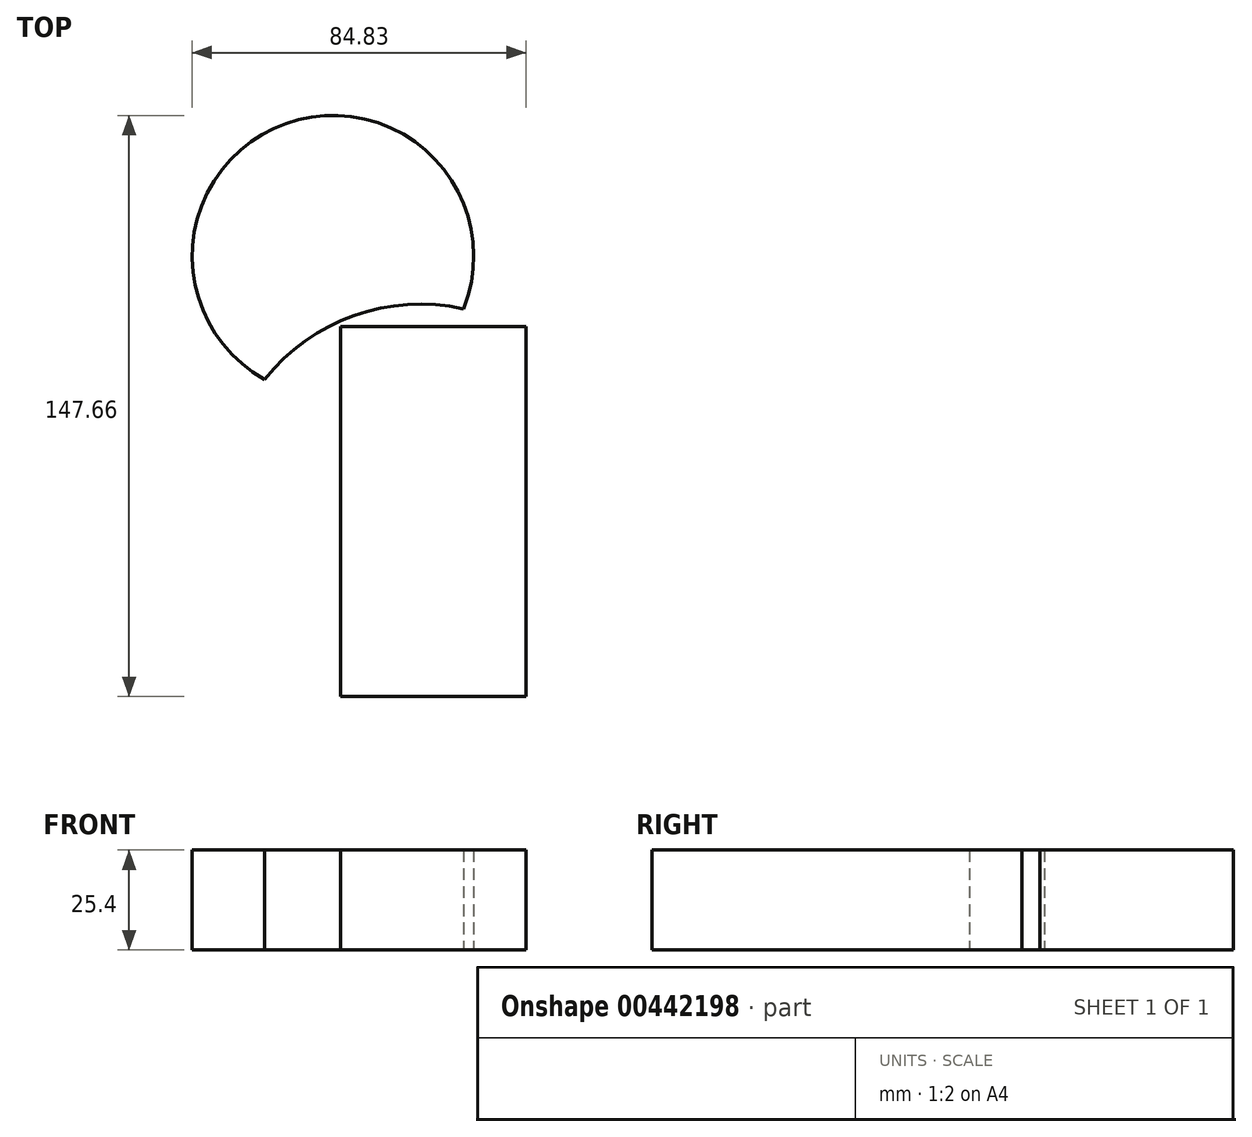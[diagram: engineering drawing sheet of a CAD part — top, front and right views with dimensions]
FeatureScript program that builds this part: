
annotation { "Feature Type Name" : "Feature", "Feature Type Description" : "" }
export const myFeature = defineFeature(function(context is Context, id is Id, definition is map)
    precondition{}
    {
        {
            var Q0;
            Q0=qCreatedBy(makeId("Top.planeOp"),FACE);
            var sketch = newSketch(context, id + "F0", { "sketchPlane" : qUnion([Q0])});
            skLineSegment(sketch, "E0.bottom", {"start": v(18.8, -30.2) * mm, "end": v(65.98, -30.2) * mm});
            skLineSegment(sketch, "E0.top", {"start": v(18.8, 63.82) * mm, "end": v(65.98, 63.82) * mm});
            skLineSegment(sketch, "E0.left", {"start": v(18.8, -30.2) * mm, "end": v(18.8, 63.82) * mm});
            skLineSegment(sketch, "E0.right", {"start": v(65.98, -30.2) * mm, "end": v(65.98, 63.82) * mm});
            skSolve(sketch);
        }
        {
            var Q0;
            Q0=makeQuery(id+"F0.imprint","IMPRINT",FACE,{"disambiguationData":[TD([[makeQuery(id+"F0.imprint","IMPRINT",EDGE,{"derivedFrom":sQuery(id+"F0.wireOp",EDGE,"E0.bottom")}),1.0]])]});
            extrude(context, id + "F1", {"entities" : qUnion([Q0]), "depth" : 25.4 * mm, "offsetDistance" : 25.4 * mm});
        }
        {
            var Q0;
            Q0=qCreatedBy(makeId("Top.planeOp"),FACE);
            var sketch = newSketch(context, id + "F2", { "sketchPlane" : qUnion([Q0])});
            skCircle(sketch, "E1", {"center": v(39.17, 18.95) * mm, "radius": 50.57 * mm});
            skCircle(sketch, "E2", {"center": v(16.91, 81.7) * mm, "radius": 35.77 * mm});
            skSolve(sketch);
        }
        {
            var Q0;
            {var subQ0=sQuery(id+"F2.wireOp",EDGE,"E2");var subQ1=sQuery(id+"F2.wireOp",EDGE,"E1");var subQ2=makeQuery(id+"F2.imprint","INTERSECT",VERTEX,{"disambiguationData":[OD(0.0)],"derivedFrom":[subQ1,subQ0]});Q0=makeQuery(id+"F2.imprint","IMPRINT",FACE,{"disambiguationData":[TD([[makeQuery(id+"F2.imprint","IMPRINT",EDGE,{"disambiguationData":[TD([[subQ2,1.0]])],"derivedFrom":subQ1}),-1.0]])]});}
            extrude(context, id + "F3", {"entities" : qUnion([Q0]), "depth" : 25.4 * mm, "offsetDistance" : 25.4 * mm});
        }
    });
